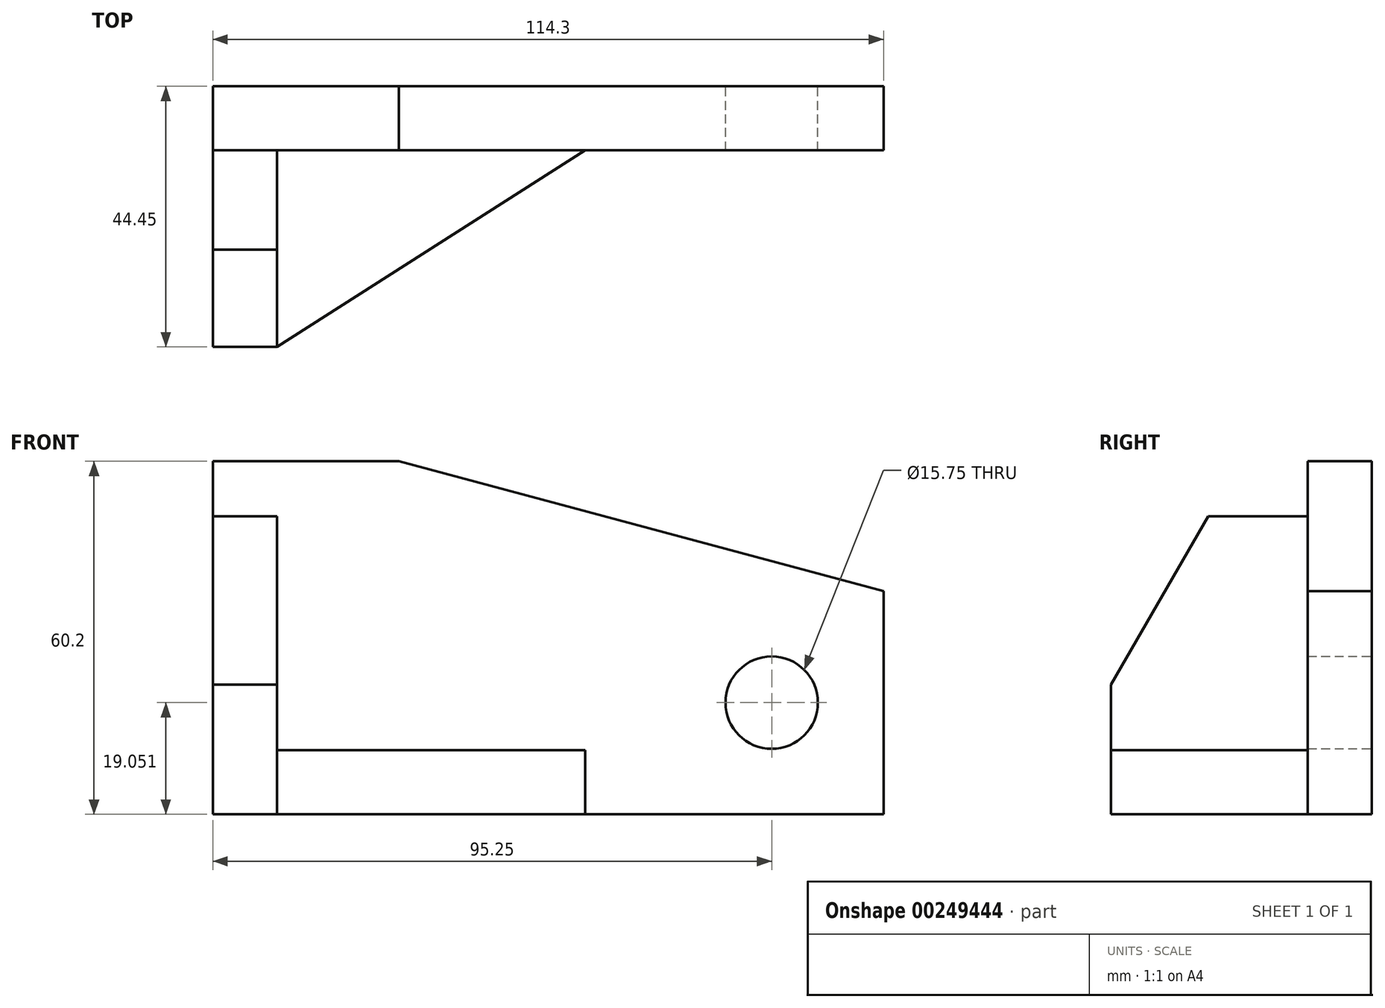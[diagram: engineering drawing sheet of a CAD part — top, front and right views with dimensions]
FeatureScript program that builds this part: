
annotation { "Feature Type Name" : "Feature", "Feature Type Description" : "" }
export const myFeature = defineFeature(function(context is Context, id is Id, definition is map)
    precondition{}
    {
        {
            var Q0;
            Q0=qCreatedBy(makeId("Front.planeOp"),FACE);
            var sketch = newSketch(context, id + "F0", { "sketchPlane" : qUnion([Q0])});
            skLineSegment(sketch, "E0.bottom", {"start": v(57.15, -30.1) * mm, "end": v(-57.15, -30.1) * mm});
            skLineSegment(sketch, "E0.top", {"start": v(-25.4, 30.1) * mm, "end": v(-57.15, 30.1) * mm});
            skLineSegment(sketch, "E0.left", {"start": v(57.15, -30.1) * mm, "end": v(57.15, 7.98) * mm});
            skLineSegment(sketch, "E0.right", {"start": v(-57.15, -30.1) * mm, "end": v(-57.15, 30.1) * mm});
            skPoint(sketch, "E0.middle", {"position": v(0, 0) * mm});
            skLineSegment(sketch, "E1", {"start": v(-25.4, 30.1) * mm, "end": v(57.15, 7.98) * mm});
            skPoint(sketch, "E2.orphan", {"position": v(57.15, 30.1) * mm});
            skCircle(sketch, "E3", {"center": v(38.1, -11.05) * mm, "radius": 7.87 * mm});
            skLineSegment(sketch, "E4", {"start": v(-57.15, 20.7) * mm, "end": v(-46.23, 20.7) * mm});
            skLineSegment(sketch, "E5", {"start": v(-46.23, 20.7) * mm, "end": v(-46.23, -30.1) * mm});
            skLineSegment(sketch, "E6", {"start": v(-46.23, -19.18) * mm, "end": v(6.35, -19.18) * mm});
            skLineSegment(sketch, "E7", {"start": v(6.35, -19.18) * mm, "end": v(6.35, -30.1) * mm});
            skSolve(sketch);
        }
        {
            var Q0;
            {var subQ1=sQuery(id+"F0.wireOp",EDGE,"E4");Q0=makeQuery(id+"F0.imprint","IMPRINT",FACE,{"disambiguationData":[TD([[makeQuery(id+"F0.imprint","IMPRINT",EDGE,{"derivedFrom":subQ1}),-1.0]])]});}
            var Q1;
            {var subQ4=sQuery(id+"F0.wireOp",EDGE,"E6");Q1=makeQuery(id+"F0.imprint","IMPRINT",FACE,{"disambiguationData":[TD([[makeQuery(id+"F0.imprint","IMPRINT",EDGE,{"derivedFrom":subQ4}),-1.0]])]});}
            var Q2;
            {var subQ1=sQuery(id+"F0.wireOp",EDGE,"E0.top");Q2=makeQuery(id+"F0.imprint","IMPRINT",FACE,{"disambiguationData":[TD([[makeQuery(id+"F0.imprint","IMPRINT",EDGE,{"derivedFrom":subQ1}),1.0]])]});}
            extrude(context, id + "F1", {"entities" : qUnion([Q0, Q1, Q2]), "depth" : 10.92 * mm});
        }
        {
            var Q0;
            {var subQ1=sQuery(id+"F0.wireOp",EDGE,"E4");Q0=makeQuery(id+"F0.imprint","IMPRINT",FACE,{"disambiguationData":[TD([[makeQuery(id+"F0.imprint","IMPRINT",EDGE,{"derivedFrom":subQ1}),-1.0]])]});}
            extrude(context, id + "F2", {"entities" : qUnion([Q0]), "operationType" : NewBodyOperationType.ADD, "depth" : 44.45 * mm});
        }
        {
            var Q0;
            {var subQ4=sQuery(id+"F0.wireOp",EDGE,"E6");Q0=makeQuery(id+"F0.imprint","IMPRINT",FACE,{"disambiguationData":[TD([[makeQuery(id+"F0.imprint","IMPRINT",EDGE,{"derivedFrom":subQ4}),-1.0]])]});}
            extrude(context, id + "F3", {"entities" : qUnion([Q0]), "operationType" : NewBodyOperationType.ADD, "depth" : 44.45 * mm});
        }
        {
            var Q0;
            Q0=makeQuery(id+"F3.opExtrude","SWEPT_FACE",FACE,{"disambiguationData":[OSD([sQuery(id+"F0.wireOp",EDGE,"E6")])]});
            var sketch = newSketch(context, id + "F4", { "sketchPlane" : qUnion([Q0])});
            skLineSegment(sketch, "E8", {"start": v(-46.23, -44.45) * mm, "end": v(6.35, -10.92) * mm});
            skSolve(sketch);
        }
        {
            var Q0;
            Q0=makeQuery(id+"F4.imprint","IMPRINT",FACE,{"disambiguationData":[TD([[makeQuery(id+"F4.imprint","IMPRINT",EDGE,{"derivedFrom":sQuery(id+"F4.wireOp",EDGE,"E8")}),-1.0]])]});
            extrude(context, id + "F5", {"entities" : qUnion([Q0]), "operationType" : NewBodyOperationType.REMOVE, "oppositeDirection" : true, "depth" : 10.92 * mm});
        }
        {
            var Q0;
            Q0=makeQuery(id+"F2.opExtrude","SWEPT_FACE",FACE,{"disambiguationData":[OSD([sQuery(id+"F0.wireOp",EDGE,"E5")])]});
            var sketch = newSketch(context, id + "F6", { "sketchPlane" : qUnion([Q0])});
            skLineSegment(sketch, "E9", {"start": v(-27.88, 20.7) * mm, "end": v(-44.45, -8) * mm});
            skSolve(sketch);
        }
        {
            var Q0;
            {var subQ0=sQuery(id+"F6.wireOp",EDGE,"E9");Q0=makeQuery(id+"F6.imprint","IMPRINT",FACE,{"disambiguationData":[TD([[makeQuery(id+"F6.imprint","IMPRINT",EDGE,{"derivedFrom":subQ0}),-1.0]])]});}
            extrude(context, id + "F7", {"entities" : qUnion([Q0]), "operationType" : NewBodyOperationType.REMOVE, "oppositeDirection" : true, "depth" : 10.92 * mm});
        }
    });
